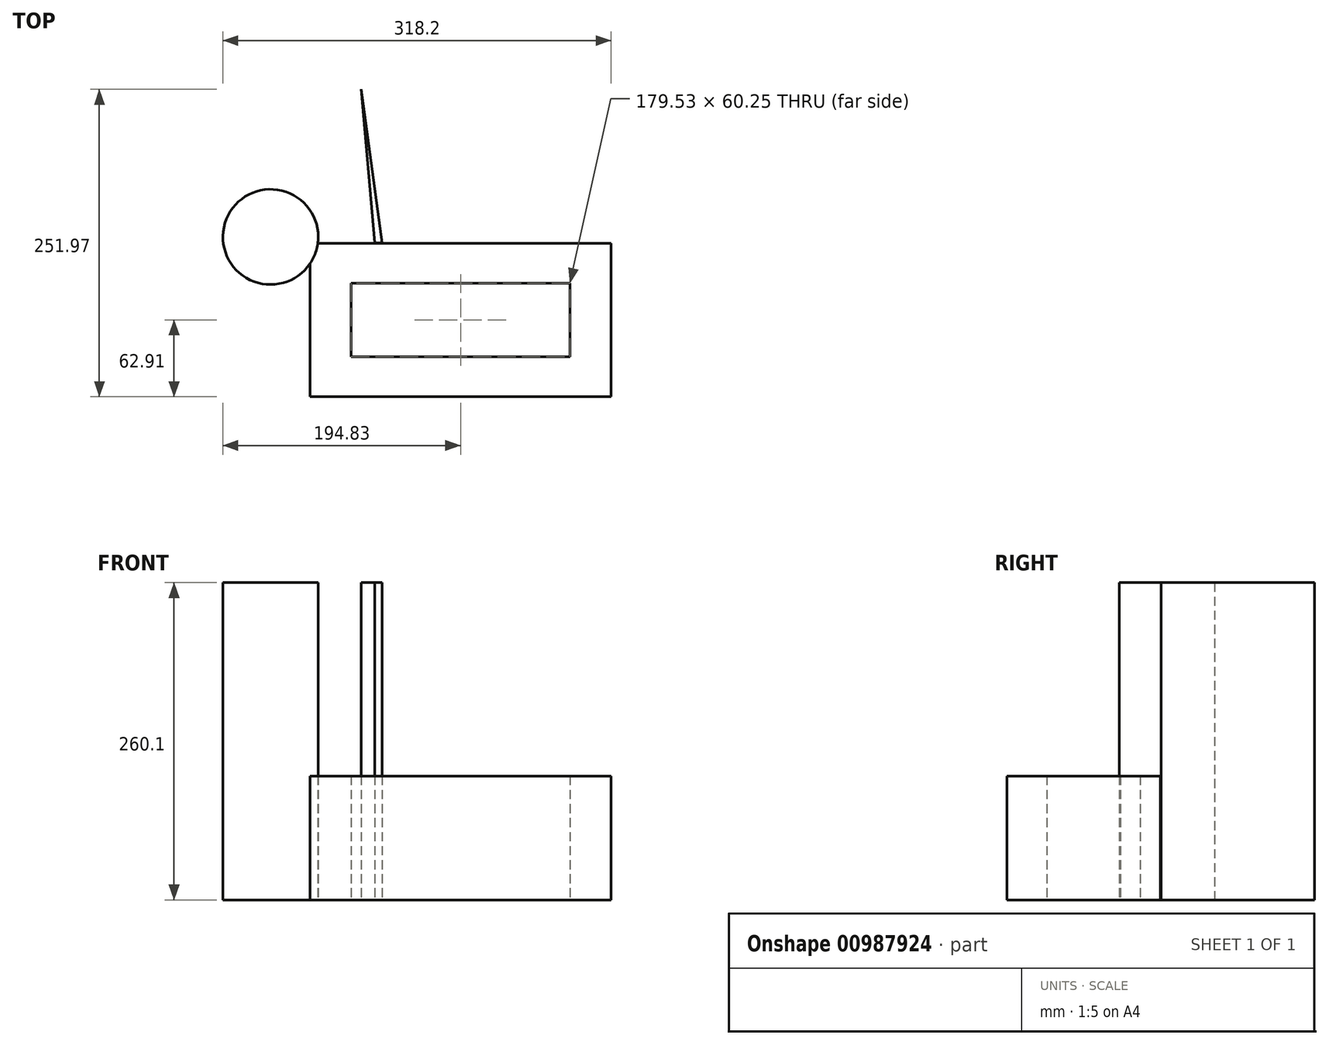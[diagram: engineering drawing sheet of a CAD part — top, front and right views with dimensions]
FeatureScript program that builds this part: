
annotation { "Feature Type Name" : "Feature", "Feature Type Description" : "" }
export const myFeature = defineFeature(function(context is Context, id is Id, definition is map)
    precondition{}
    {
        {
            var Q0;
            Q0=qCreatedBy(makeId("Top.planeOp"),FACE);
            var sketch = newSketch(context, id + "F0", { "sketchPlane" : qUnion([Q0])});
            skLineSegment(sketch, "E0.bottom", {"start": v(-123.37, 62.91) * mm, "end": v(123.37, 62.91) * mm});
            skLineSegment(sketch, "E0.top", {"start": v(-123.37, -62.91) * mm, "end": v(123.37, -62.91) * mm});
            skLineSegment(sketch, "E0.left", {"start": v(-123.37, 62.91) * mm, "end": v(-123.37, -62.91) * mm});
            skLineSegment(sketch, "E0.right", {"start": v(123.37, 62.91) * mm, "end": v(123.37, -62.91) * mm});
            skPoint(sketch, "E0.middle", {"position": v(0, 0) * mm});
            skLineSegment(sketch, "E1.bottom", {"start": v(-89.77, 30.13) * mm, "end": v(89.77, 30.13) * mm});
            skLineSegment(sketch, "E1.top", {"start": v(-89.77, -30.13) * mm, "end": v(89.77, -30.13) * mm});
            skLineSegment(sketch, "E1.left", {"start": v(-89.77, 30.13) * mm, "end": v(-89.77, -30.13) * mm});
            skLineSegment(sketch, "E1.right", {"start": v(89.77, 30.13) * mm, "end": v(89.77, -30.13) * mm});
            skSolve(sketch);
        }
        {
            var Q0;
            Q0 = qSketchRegion(id + "F0", true);
            extrude(context, id + "F1", {"entities" : qUnion([Q0]), "depth" : 101.6 * mm, "offsetDistance" : 25.4 * mm});
        }
        {
            var Q0;
            Q0=qCreatedBy(makeId("Top.planeOp"),FACE);
            var sketch = newSketch(context, id + "F2", { "sketchPlane" : qUnion([Q0])});
            skCircle(sketch, "E2", {"center": v(0, 0) * mm, "radius": 20.36 * mm});
            skLineSegment(sketch, "E3", {"start": v(-59.18, -62.64) * mm, "end": v(-75.28, 63.4) * mm});
            skLineSegment(sketch, "E4", {"start": v(-75.28, 63.4) * mm, "end": v(-59.18, -62.64) * mm});
            skLineSegment(sketch, "E5", {"start": v(-59.18, -62.64) * mm, "end": v(-59.18, -62.64) * mm});
            skLineSegment(sketch, "E6", {"start": v(-64.47, 63.3) * mm, "end": v(-81.65, 189.06) * mm});
            skLineSegment(sketch, "E7", {"start": v(-81.65, 189.06) * mm, "end": v(-59.18, -62.64) * mm});
            skLineSegment(sketch, "E8", {"start": v(-75.28, 63.4) * mm, "end": v(-64.47, 63.3) * mm});
            skSolve(sketch);
        }
        {
            var Q0;
            Q0=qCreatedBy(makeId("Top.planeOp"),FACE);
            var sketch = newSketch(context, id + "F3", { "sketchPlane" : qUnion([Q0])});
            skCircle(sketch, "E9", {"center": v(-155.78, 68.1) * mm, "radius": 39.06 * mm});
            skCircle(sketch, "E10", {"center": v(-155.78, 68.1) * mm, "radius": 15.62 * mm});
            skSolve(sketch);
        }
        {
            var Q0;
            Q0=makeQuery(id+"F3.imprint","IMPRINT",FACE,{"disambiguationData":[TD([[makeQuery(id+"F3.imprint","IMPRINT",EDGE,{"derivedFrom":sQuery(id+"F3.wireOp",EDGE,"E9")}),1.0]])]});
            var Q1;
            Q1=makeQuery(id+"F3.imprint","IMPRINT",FACE,{"disambiguationData":[TD([[makeQuery(id+"F3.imprint","IMPRINT",EDGE,{"derivedFrom":sQuery(id+"F3.wireOp",EDGE,"E10")}),1.0]])]});
            var Q2;
            {var subQ0=sQuery(id+"F2.wireOp",EDGE,"E6");Q2=makeQuery(id+"F2.imprint","IMPRINT",FACE,{"disambiguationData":[TD([[makeQuery(id+"F2.imprint","IMPRINT",EDGE,{"derivedFrom":subQ0}),1.0]])]});}
            extrude(context, id + "F4", {"entities" : qUnion([Q0, Q1, Q2]), "operationType" : NewBodyOperationType.ADD, "depth" : 260.1 * mm, "offsetDistance" : 25.4 * mm});
        }
    });
